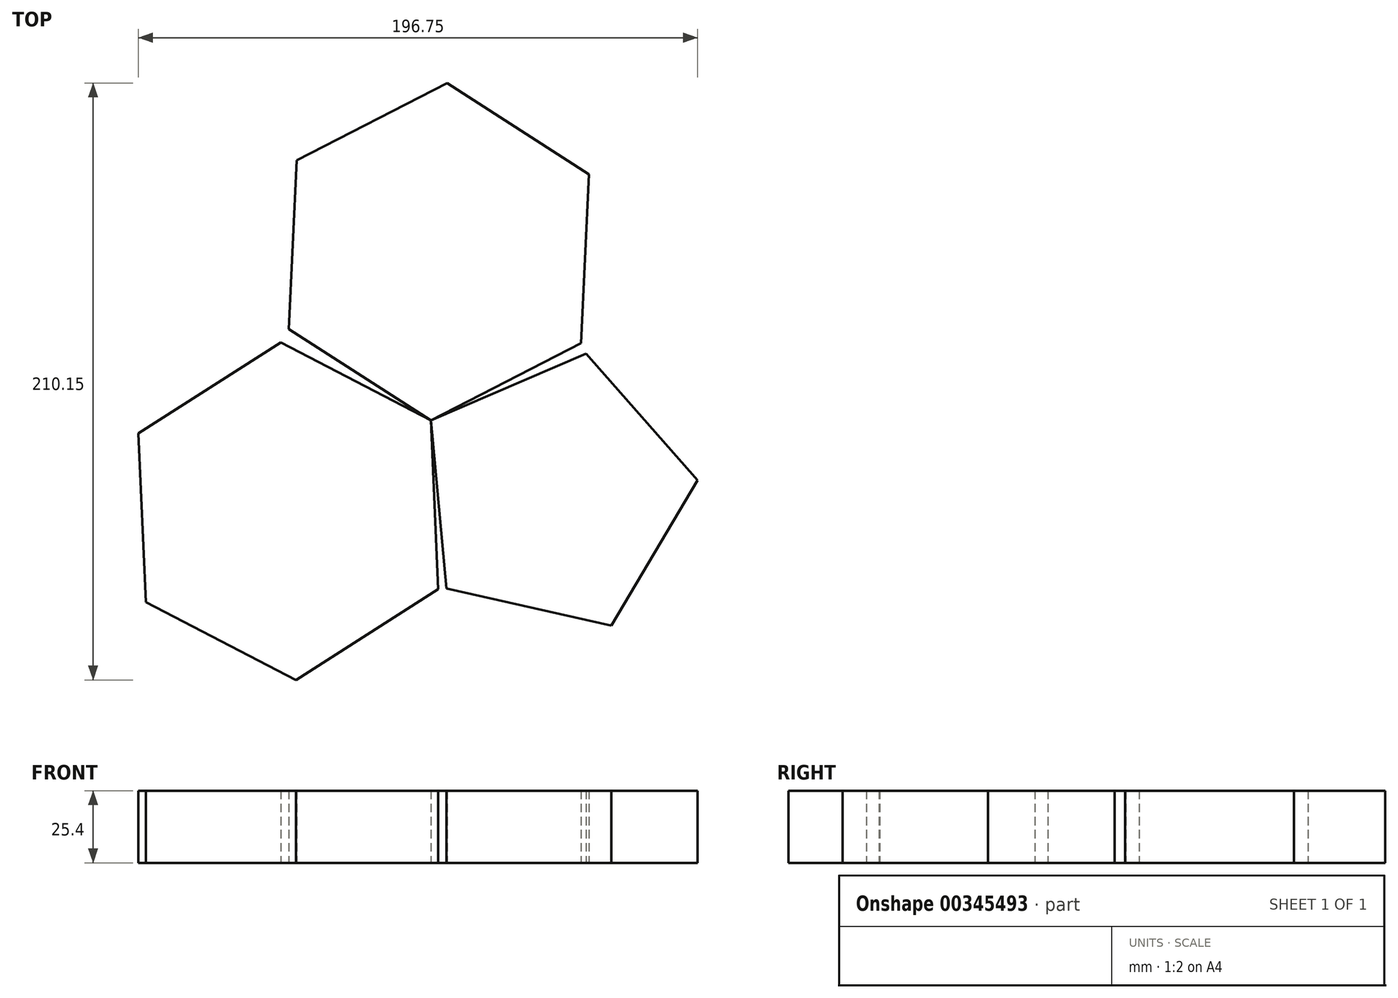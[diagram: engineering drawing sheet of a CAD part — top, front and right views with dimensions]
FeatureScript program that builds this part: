
annotation { "Feature Type Name" : "Feature", "Feature Type Description" : "" }
export const myFeature = defineFeature(function(context is Context, id is Id, definition is map)
    precondition{}
    {
        {
            var Q0;
            Q0=qCreatedBy(makeId("Top.planeOp"),FACE);
            var sketch = newSketch(context, id + "F0", { "sketchPlane" : qUnion([Q0])});
            skCircle(sketch, "E0", {"center": v(0, 0) * mm, "radius": 31.68 * mm});
            skCircle(sketch, "E1.cCircle", {"center": v(-50.13, -31.97) * mm, "radius": 51.5 * mm, "construction": true});
            skLineSegment(sketch, "E1.0", {"start": v(0, 0) * mm, "end": v(2.62, -59.4) * mm});
            skLineSegment(sketch, "E1.1", {"start": v(2.62, -59.4) * mm, "end": v(-47.5, -91.37) * mm});
            skLineSegment(sketch, "E1.2", {"start": v(-47.5, -91.37) * mm, "end": v(-100.26, -63.95) * mm});
            skLineSegment(sketch, "E1.3", {"start": v(-100.26, -63.95) * mm, "end": v(-102.89, -4.55) * mm});
            skLineSegment(sketch, "E1.4", {"start": v(-102.89, -4.55) * mm, "end": v(-52.76, 27.43) * mm});
            skLineSegment(sketch, "E1.5", {"start": v(-52.76, 27.43) * mm, "end": v(0, 0) * mm});
            skPoint(sketch, "E1.0.midPoint", {"position": v(1.31, -29.7) * mm});
            skCircle(sketch, "E2.cCircle", {"center": v(2.85, 59.4) * mm, "radius": 51.5 * mm, "construction": true});
            skLineSegment(sketch, "E2.0", {"start": v(-50, 32.16) * mm, "end": v(0, 0) * mm});
            skLineSegment(sketch, "E2.1", {"start": v(-47.16, 91.56) * mm, "end": v(-50, 32.16) * mm});
            skLineSegment(sketch, "E2.2", {"start": v(-47.16, 91.56) * mm, "end": v(5.7, 118.78) * mm});
            skLineSegment(sketch, "E2.3", {"start": v(55.71, 86.62) * mm, "end": v(5.7, 118.78) * mm});
            skLineSegment(sketch, "E2.4", {"start": v(52.86, 27.23) * mm, "end": v(55.71, 86.62) * mm});
            skLineSegment(sketch, "E2.5", {"start": v(52.86, 27.23) * mm, "end": v(0, 0) * mm});
            skPoint(sketch, "E2.0.midPoint", {"position": v(-25, 16.08) * mm});
            skCircle(sketch, "E3.cCircle", {"center": v(43.5, -25.8) * mm, "radius": 40.92 * mm, "construction": true});
            skLineSegment(sketch, "E3.0", {"start": v(0, 0) * mm, "end": v(54.6, 23.54) * mm});
            skLineSegment(sketch, "E3.1", {"start": v(54.6, 23.54) * mm, "end": v(93.86, -21.1) * mm});
            skLineSegment(sketch, "E3.2", {"start": v(93.86, -21.1) * mm, "end": v(63.53, -72.25) * mm});
            skLineSegment(sketch, "E3.3", {"start": v(63.53, -72.25) * mm, "end": v(5.52, -59.2) * mm});
            skLineSegment(sketch, "E3.4", {"start": v(5.52, -59.2) * mm, "end": v(0, 0) * mm});
            skPoint(sketch, "E3.0.midPoint", {"position": v(27.3, 11.77) * mm});
            skSolve(sketch);
        }
        {
            var Q0;
            {var subQ0=sQuery(id+"F0.wireOp",EDGE,"E2.1");Q0=makeQuery(id+"F0.imprint","IMPRINT",FACE,{"disambiguationData":[TD([[makeQuery(id+"F0.imprint","IMPRINT",EDGE,{"derivedFrom":subQ0}),1.0]])]});}
            var Q1;
            {var subQ0=sQuery(id+"F0.wireOp",EDGE,"E1.1");Q1=makeQuery(id+"F0.imprint","IMPRINT",FACE,{"disambiguationData":[TD([[makeQuery(id+"F0.imprint","IMPRINT",EDGE,{"derivedFrom":subQ0}),-1.0]])]});}
            var Q2;
            {var subQ0=sQuery(id+"F0.wireOp",EDGE,"E3.1");Q2=makeQuery(id+"F0.imprint","IMPRINT",FACE,{"disambiguationData":[TD([[makeQuery(id+"F0.imprint","IMPRINT",EDGE,{"derivedFrom":subQ0}),-1.0]])]});}
            var Q3;
            {var subQ0=sQuery(id+"F0.wireOp",EDGE,"E1.5");var subQ1=sQuery(id+"F0.wireOp",EDGE,"E0");var subQ2=makeQuery(id+"F0.imprint","INTERSECT",VERTEX,{"derivedFrom":[subQ1,subQ0]});Q3=makeQuery(id+"F0.imprint","IMPRINT",FACE,{"disambiguationData":[TD([[makeQuery(id+"F0.imprint","IMPRINT",EDGE,{"disambiguationData":[TD([[subQ2,-1.0]])],"derivedFrom":subQ1}),1.0]])]});}
            var Q4;
            {var subQ0=sQuery(id+"F0.wireOp",EDGE,"E2.5");var subQ1=sQuery(id+"F0.wireOp",EDGE,"E0");var subQ2=makeQuery(id+"F0.imprint","INTERSECT",VERTEX,{"derivedFrom":[subQ1,subQ0]});Q4=makeQuery(id+"F0.imprint","IMPRINT",FACE,{"disambiguationData":[TD([[makeQuery(id+"F0.imprint","IMPRINT",EDGE,{"disambiguationData":[TD([[subQ2,-1.0]])],"derivedFrom":subQ1}),1.0]])]});}
            var Q5;
            {var subQ0=sQuery(id+"F0.wireOp",EDGE,"E3.0");var subQ1=sQuery(id+"F0.wireOp",EDGE,"E0");var subQ2=makeQuery(id+"F0.imprint","INTERSECT",VERTEX,{"derivedFrom":[subQ1,subQ0]});Q5=makeQuery(id+"F0.imprint","IMPRINT",FACE,{"disambiguationData":[TD([[makeQuery(id+"F0.imprint","IMPRINT",EDGE,{"disambiguationData":[TD([[subQ2,1.0]])],"derivedFrom":subQ1}),1.0]])]});}
            extrude(context, id + "F1", {"entities" : qUnion([Q0, Q1, Q2, Q3, Q4, Q5]), "depth" : 25.4 * mm});
        }
    });
